# Revit family: S 0415 FLC-M2
name_source: partatom
category: Lighting Fixtures
revit_build: Autodesk Revit 2017 (Build: 20160225_1515(x64)
units: mm (PartAtom-declared; Revit-internal decimal feet)

## family parameters
Cut with Voids When Loaded = No
Host = Face
Light Source = Yes
Part Type = Normal
Room Calculation Point = No
Round Connector Dimension = Use Diameter
Shared = No

## types (3) — shared parameters
Beam Angle = 66.00°
Color Filter = 16777215
Default Elevation = 1219 mm
Dimming Lamp Color Temperature Shift = <None>
Emit Shape Visible in Rendering = Yes
Emit from Circle Diameter = 270 mm  [stored 0.885827 ft]
Light Source Symbol Size = 610 mm
Manufacturer = ARLIGHT
Type Image = S 0415 FLC-M2.JPG

## per-type parameters (varying)
| type | Apparent Load | Wattage Comments |
| SFLS.415.150.M2.40.66 | 150 VA | 150W |
| SFLS.415.180.M2.40.66 | 180 VA | 180W |
| SFLS.415.105.M2.40.66 | 105 VA | 105W |

note: [stored X ft] marks values corroborated as IEEE doubles in the binary element streams (Revit-internal decimal feet)

## geometry (parser evidence)
native form markers: Sweep x3
no freeform markers — native parametric forms only
